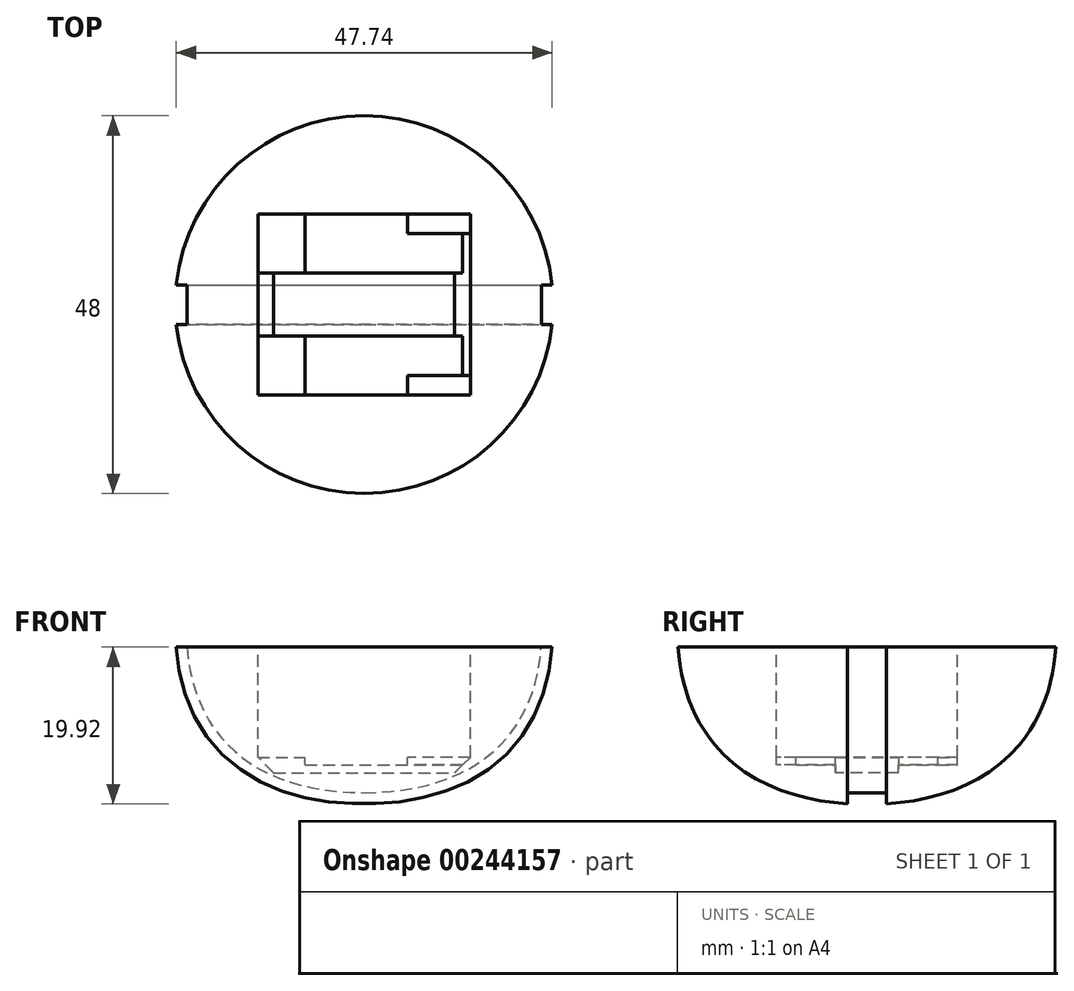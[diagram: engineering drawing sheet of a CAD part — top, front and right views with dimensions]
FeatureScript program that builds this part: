
annotation { "Feature Type Name" : "Feature", "Feature Type Description" : "" }
export const myFeature = defineFeature(function(context is Context, id is Id, definition is map)
    precondition{}
    {
        {
            var Q0;
            Q0=qCreatedBy(makeId("Front.planeOp"),FACE);
            var sketch = newSketch(context, id + "F0", { "sketchPlane" : qUnion([Q0])});
            skLineSegment(sketch, "E0", {"start": v(0, 0) * mm, "end": v(0, 60) * mm});
            skLineSegment(sketch, "E1", {"start": v(0, 0) * mm, "end": v(0, 20) * mm, "construction": true});
            skLineSegment(sketch, "E2", {"start": v(0, 20) * mm, "end": v(24, 20) * mm});
            skLineSegment(sketch, "E3", {"start": v(0, 60) * mm, "end": v(14, 60) * mm, "construction": true});
            skLineSegment(sketch, "E4", {"start": v(0, 0) * mm, "end": v(14, 0) * mm, "construction": true});
            skFitSpline(sketch, "E5", {"points": [v(0, 0) * mm, v(24, 20) * mm, v(0, 60) * mm], "startDerivative": vector(93.32, 0) * mm, "endDerivative": vector(-76.37, 0) * mm});
            skFitSpline(sketch, "E6.MirrorCS", {"points": [v(0, 0) * mm, v(-24, 20) * mm, v(0, 60) * mm], "startDerivative": vector(-93.32, 0) * mm, "endDerivative": vector(76.37, 0) * mm});
            skSolve(sketch);
        }
        {
            var Q0;
            {var subQ3=sQuery(id+"F0.wireOp",EDGE,"E2");Q0=makeQuery(id+"F0.imprint","IMPRINT",FACE,{"disambiguationData":[TD([[makeQuery(id+"F0.imprint","IMPRINT",EDGE,{"derivedFrom":subQ3}),-1.0]])]});}
            var Q1;
            Q1=sQuery(id+"F0.wireOp",EDGE,"E0");
            revolve(context, id + "F1", {"entities" : qUnion([Q0]), "axis" : qUnion([Q1]), "revolveType" : RevolveType.FULL});
        }
        {
            var Q0;
            Q0=makeQuery(id+"F1.opRevolve","SWEPT_FACE",FACE,{"disambiguationData":[OSD([sQuery(id+"F0.wireOp",EDGE,"E2")])]});
            var sketch = newSketch(context, id + "F2", { "sketchPlane" : qUnion([Q0])});
            skLineSegment(sketch, "E7", {"start": v(0, 0) * mm, "end": v(13.5, 0) * mm, "construction": true});
            skLineSegment(sketch, "E8", {"start": v(13.5, 0) * mm, "end": v(13.5, 11.5) * mm});
            skLineSegment(sketch, "E9", {"start": v(13.5, 11.5) * mm, "end": v(-13.5, 11.5) * mm});
            skLineSegment(sketch, "E10", {"start": v(-13.5, 11.5) * mm, "end": v(-13.5, -11.5) * mm});
            skLineSegment(sketch, "E11", {"start": v(-13.5, -11.5) * mm, "end": v(13.5, -11.5) * mm});
            skLineSegment(sketch, "E12", {"start": v(13.5, -11.5) * mm, "end": v(13.5, 0) * mm});
            skSolve(sketch);
        }
        {
            var Q0;
            Q0=makeQuery(id+"F2.imprint","IMPRINT",FACE,{"disambiguationData":[TD([[makeQuery(id+"F2.imprint","IMPRINT",EDGE,{"derivedFrom":sQuery(id+"F2.wireOp",EDGE,"E8")}),1.0]])]});
            var Q1;
            Q1 = qConstructionFilter(qBodyType(qCreatedBy(id + "F2" ,EDGE), BodyType.WIRE), ConstructionObject.NO);
            extrude(context, id + "F3", {"entities" : qUnion([Q0]), "operationType" : NewBodyOperationType.REMOVE, "surfaceEntities" : qUnion([Q1]), "oppositeDirection" : true, "depth" : 14 * mm});
        }
        {
            var Q0;
            Q0=makeQuery(id+"F3.boolean.opBoolean","COPY",FACE,{"derivedFrom":makeQuery(id+"F3.opExtrude","CAP_FACE",FACE,{"disambiguationData":[OSD([sQuery(id+"F2.wireOp",EDGE,"E8"),sQuery(id+"F2.wireOp",EDGE,"E9"),sQuery(id+"F2.wireOp",EDGE,"E10"),sQuery(id+"F2.wireOp",EDGE,"E11"),sQuery(id+"F2.wireOp",EDGE,"E12")])],"isStart":false})});
            var sketch = newSketch(context, id + "F4", { "sketchPlane" : qUnion([Q0])});
            skLineSegment(sketch, "E13", {"start": v(13.5, 0) * mm, "end": v(5.5, 0) * mm, "construction": true});
            skPoint(sketch, "E13.endSnap0", {"position": v(13.5, 0) * mm});
            skLineSegment(sketch, "E14", {"start": v(5.5, 9) * mm, "end": v(5.5, 11.5) * mm});
            skLineSegment(sketch, "E15", {"start": v(5.5, 11.5) * mm, "end": v(-7.5, 11.5) * mm});
            skLineSegment(sketch, "E16", {"start": v(-7.5, 11.5) * mm, "end": v(-7.5, -11.5) * mm});
            skLineSegment(sketch, "E17", {"start": v(-7.5, -11.5) * mm, "end": v(5.5, -11.5) * mm});
            skLineSegment(sketch, "E18", {"start": v(5.5, -9) * mm, "end": v(5.5, -11.5) * mm});
            skLineSegment(sketch, "E19", {"start": v(13.5, 0) * mm, "end": v(13.5, -9) * mm});
            skLineSegment(sketch, "E20", {"start": v(13.5, -9) * mm, "end": v(5.5, -9) * mm});
            skLineSegment(sketch, "E21", {"start": v(13.5, 0) * mm, "end": v(13.5, 9) * mm});
            skLineSegment(sketch, "E22", {"start": v(13.5, 9) * mm, "end": v(5.5, 9) * mm});
            skSolve(sketch);
        }
        {
            var Q0;
            Q0 = qSketchRegion(id + "F4", true);
            extrude(context, id + "F5", {"entities" : qUnion([Q0]), "operationType" : NewBodyOperationType.REMOVE, "oppositeDirection" : true, "depth" : 1 * mm});
        }
        {
            var Q0;
            Q0=makeQuery(id+"F5.boolean.opBoolean","COPY",FACE,{"derivedFrom":makeQuery(id+"F5.opExtrude","CAP_FACE",FACE,{"disambiguationData":[OSD([sQuery(id+"F4.wireOp",EDGE,"E14"),sQuery(id+"F4.wireOp",EDGE,"E15"),sQuery(id+"F4.wireOp",EDGE,"E16"),sQuery(id+"F4.wireOp",EDGE,"E17"),sQuery(id+"F4.wireOp",EDGE,"E18"),sQuery(id+"F4.wireOp",EDGE,"E19"),sQuery(id+"F4.wireOp",EDGE,"E20"),sQuery(id+"F4.wireOp",EDGE,"E21"),sQuery(id+"F4.wireOp",EDGE,"E22")])],"isStart":false})});
            var sketch = newSketch(context, id + "F6", { "sketchPlane" : qUnion([Q0])});
            skLineSegment(sketch, "E23", {"start": v(13.5, 0) * mm, "end": v(13.5, 4) * mm});
            skLineSegment(sketch, "E24", {"start": v(13.5, 4) * mm, "end": v(-13.5, 4) * mm});
            skLineSegment(sketch, "E25", {"start": v(-13.5, 4) * mm, "end": v(-13.5, -4) * mm});
            skLineSegment(sketch, "E26", {"start": v(-13.5, -4) * mm, "end": v(13.5, -4) * mm});
            skLineSegment(sketch, "E27", {"start": v(13.5, -4) * mm, "end": v(13.5, 0) * mm});
            skSolve(sketch);
        }
        {
            var Q0;
            Q0 = qSketchRegion(id + "F6", true);
            extrude(context, id + "F7", {"entities" : qUnion([Q0]), "operationType" : NewBodyOperationType.REMOVE, "oppositeDirection" : true, "depth" : 1 * mm, "hasSecondDirection" : true, "secondDirectionOppositeDirection" : false, "secondDirectionDepth" : 1 * mm});
        }
        {
            var Q0;
            Q0=qCreatedBy(makeId("Right.planeOp"),FACE);
            var sketch = newSketch(context, id + "F8", { "sketchPlane" : qUnion([Q0])});
            skLineSegment(sketch, "E28", {"start": v(0, 0) * mm, "end": v(2.5, 0) * mm});
            skLineSegment(sketch, "E29", {"start": v(2.5, 0) * mm, "end": v(2.5, 1.5) * mm});
            skLineSegment(sketch, "E30", {"start": v(2.5, 1.5) * mm, "end": v(-2.5, 1.5) * mm});
            skLineSegment(sketch, "E31", {"start": v(-2.5, 1.5) * mm, "end": v(-2.5, 0) * mm});
            skLineSegment(sketch, "E32", {"start": v(-2.5, 0) * mm, "end": v(0, 0) * mm});
            skSolve(sketch);
        }
        {
            var Q0;
            Q0=makeQuery(id+"F7.boolean.opBoolean","COPY",EDGE,{"derivedFrom":makeQuery(id+"F7.opExtrude","CAP_EDGE",EDGE,{"disambiguationData":[OSD([sQuery(id+"F6.wireOp",EDGE,"E25")])],"isStart":false})});
            var Q1;
            Q1=makeQuery(id+"F7.boolean.opBoolean","COPY",EDGE,{"derivedFrom":makeQuery(id+"F7.opExtrude","CAP_EDGE",EDGE,{"disambiguationData":[OSD([sQuery(id+"F6.wireOp",EDGE,"E23"),sQuery(id+"F6.wireOp",EDGE,"E27")])],"isStart":false})});
            chamfer(context, id + "F9", {"entities" : qUnion([Q0, Q1]), "width" : 2 * mm, "tangentPropagation" : true});
        }
        {
            var Q0;
            Q0 = qSketchRegion(id + "F8", true);
            var Q1;
            Q1=sQuery(id+"F0.wireOp",EDGE,"E5");
            var Q2;
            Q2=sQuery(id+"F0.wireOp",EDGE,"E6.MirrorCS");
            sweep(context, id + "F10", {"operationType" : NewBodyOperationType.REMOVE, "profiles" : qUnion([Q0]), "path" : qUnion([Q1, Q2])});
        }
    });
